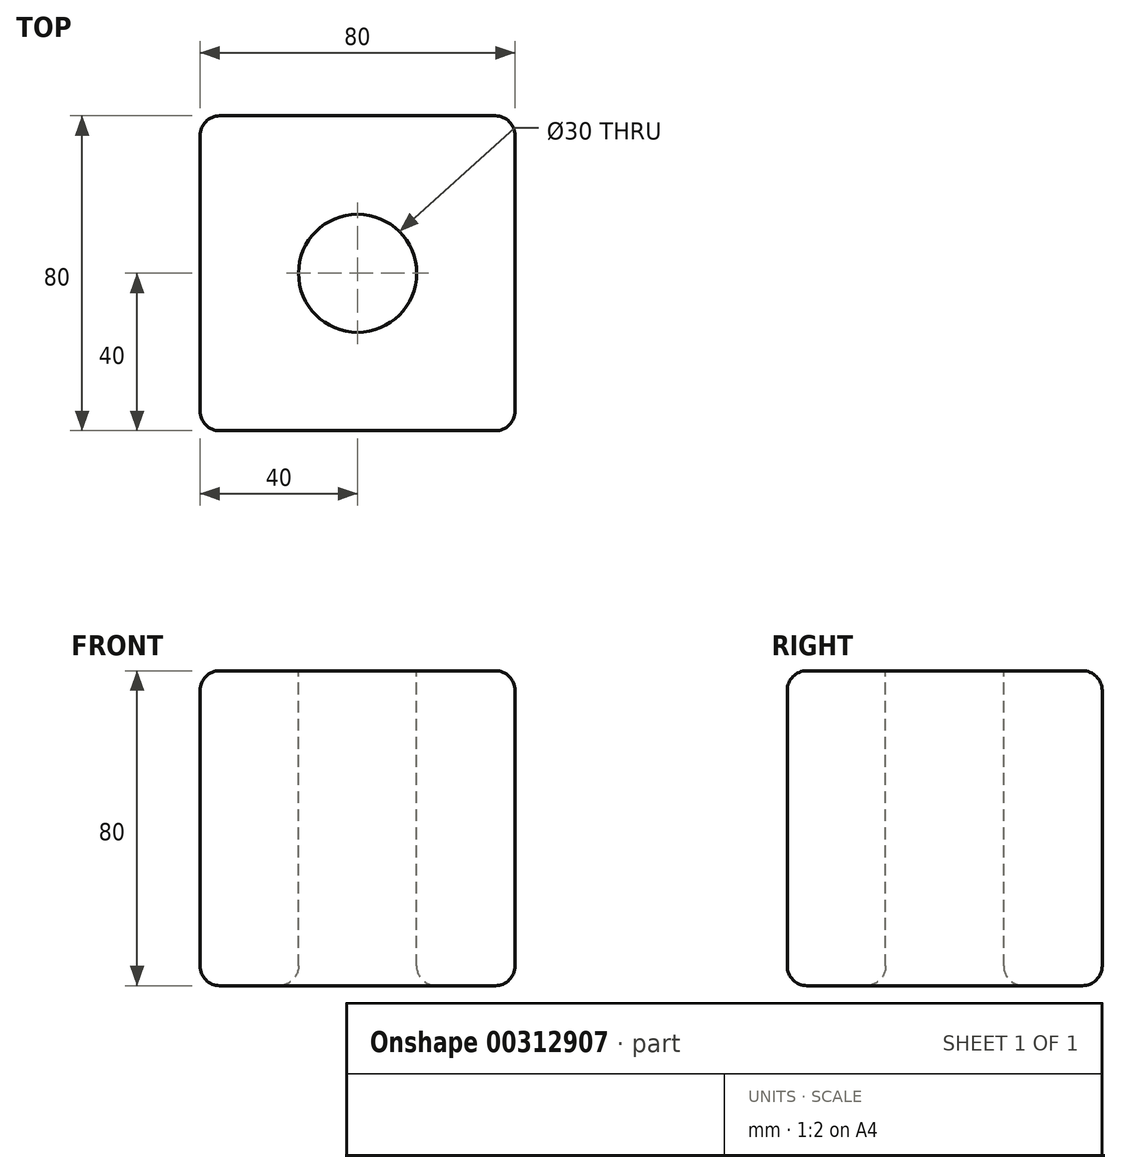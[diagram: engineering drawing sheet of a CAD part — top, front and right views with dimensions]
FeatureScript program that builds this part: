
annotation { "Feature Type Name" : "Feature", "Feature Type Description" : "" }
export const myFeature = defineFeature(function(context is Context, id is Id, definition is map)
    precondition{}
    {
        {
            var Q0;
            Q0=qCreatedBy(makeId("Top.planeOp"),FACE);
            var sketch = newSketch(context, id + "F0", { "sketchPlane" : qUnion([Q0])});
            skLineSegment(sketch, "E0.bottom", {"start": v(-40, 40) * mm, "end": v(40, 40) * mm});
            skLineSegment(sketch, "E0.top", {"start": v(-40, -40) * mm, "end": v(40, -40) * mm});
            skLineSegment(sketch, "E0.left", {"start": v(-40, 40) * mm, "end": v(-40, -40) * mm});
            skLineSegment(sketch, "E0.right", {"start": v(40, 40) * mm, "end": v(40, -40) * mm});
            skPoint(sketch, "E0.middle", {"position": v(0, 0) * mm});
            skSolve(sketch);
        }
        {
            var Q0;
            Q0 = qSketchRegion(id + "F0", true);
            extrude(context, id + "F1", {"entities" : qUnion([Q0]), "endBound" : BoundingType.SYMMETRIC, "depth" : 80 * mm});
        }
        {
            var Q0;
            Q0=makeQuery(id+"F1.opExtrude","CAP_FACE",FACE,{"disambiguationData":[OSD([sQuery(id+"F0.wireOp",EDGE,"E0.bottom"),sQuery(id+"F0.wireOp",EDGE,"E0.top"),sQuery(id+"F0.wireOp",EDGE,"E0.left"),sQuery(id+"F0.wireOp",EDGE,"E0.right")])],"isStart":false});
            var Q1;
            Q1=makeQuery(id+"F1.opExtrude","SWEPT_EDGE",EDGE,{"disambiguationData":[OSD([sQuery(id+"F0.wireOp",EDGE,"E0.top"),sQuery(id+"F0.wireOp",EDGE,"E0.left")])]});
            var Q2;
            Q2=makeQuery(id+"F1.opExtrude","CAP_EDGE",EDGE,{"disambiguationData":[OSD([sQuery(id+"F0.wireOp",EDGE,"E0.top")])],"isStart":false});
            var Q3;
            Q3=makeQuery(id+"F1.opExtrude","SWEPT_EDGE",EDGE,{"disambiguationData":[OSD([sQuery(id+"F0.wireOp",EDGE,"E0.top"),sQuery(id+"F0.wireOp",EDGE,"E0.right")])]});
            var Q4;
            Q4=makeQuery(id+"F1.opExtrude","CAP_EDGE",EDGE,{"disambiguationData":[OSD([sQuery(id+"F0.wireOp",EDGE,"E0.right")])],"isStart":true});
            var Q5;
            Q5=makeQuery(id+"F1.opExtrude","CAP_EDGE",EDGE,{"disambiguationData":[OSD([sQuery(id+"F0.wireOp",EDGE,"E0.top")])],"isStart":true});
            var Q6;
            Q6=makeQuery(id+"F1.opExtrude","CAP_EDGE",EDGE,{"disambiguationData":[OSD([sQuery(id+"F0.wireOp",EDGE,"E0.left")])],"isStart":true});
            var Q7;
            Q7=makeQuery(id+"F1.opExtrude","CAP_FACE",FACE,{"disambiguationData":[OSD([sQuery(id+"F0.wireOp",EDGE,"E0.bottom"),sQuery(id+"F0.wireOp",EDGE,"E0.top"),sQuery(id+"F0.wireOp",EDGE,"E0.left"),sQuery(id+"F0.wireOp",EDGE,"E0.right")])],"isStart":true});
            var Q8;
            Q8=makeQuery(id+"F1.opExtrude","SWEPT_EDGE",EDGE,{"disambiguationData":[OSD([sQuery(id+"F0.wireOp",EDGE,"E0.bottom"),sQuery(id+"F0.wireOp",EDGE,"E0.left")])]});
            var Q9;
            Q9=makeQuery(id+"F1.opExtrude","CAP_EDGE",EDGE,{"disambiguationData":[OSD([sQuery(id+"F0.wireOp",EDGE,"E0.bottom")])],"isStart":false});
            var Q10;
            Q10=makeQuery(id+"F1.opExtrude","SWEPT_EDGE",EDGE,{"disambiguationData":[OSD([sQuery(id+"F0.wireOp",EDGE,"E0.bottom"),sQuery(id+"F0.wireOp",EDGE,"E0.right")])]});
            fillet(context, id + "F2", {"entities" : qUnion([Q0, Q1, Q2, Q3, Q4, Q5, Q6, Q7, Q8, Q9, Q10]), "radius" : 5 * mm, "tangentPropagation" : true, "allowEdgeOverflow" : false});
        }
        {
            var Q0;
            Q0=makeQuery(id+"F1.opExtrude","CAP_FACE",FACE,{"disambiguationData":[OSD([sQuery(id+"F0.wireOp",EDGE,"E0.bottom"),sQuery(id+"F0.wireOp",EDGE,"E0.top"),sQuery(id+"F0.wireOp",EDGE,"E0.left"),sQuery(id+"F0.wireOp",EDGE,"E0.right")])],"isStart":false});
            var sketch = newSketch(context, id + "F3", { "sketchPlane" : qUnion([Q0])});
            skCircle(sketch, "E1", {"center": v(0, 0) * mm, "radius": 15 * mm});
            skSolve(sketch);
        }
        {
            var Q0;
            Q0=makeQuery(id+"F3.imprint","IMPRINT",FACE,{"disambiguationData":[TD([[makeQuery(id+"F3.imprint","IMPRINT",EDGE,{"derivedFrom":sQuery(id+"F3.wireOp",EDGE,"E1")}),1.0]])]});
            extrude(context, id + "F4", {"entities" : qUnion([Q0]), "operationType" : NewBodyOperationType.REMOVE, "endBound" : BoundingType.THROUGH_ALL, "oppositeDirection" : true, "depth" : 25 * mm});
        }
        {
            var Q0;
            Q0=makeQuery(id+"F4.boolean.opBoolean","COPY",EDGE,{"derivedFrom":makeQuery(id+"F4.opExtrude","CAP_EDGE",EDGE,{"disambiguationData":[OSD([sQuery(id+"F3.wireOp",EDGE,"E1")])],"isStart":true})});
            var Q1;
            Q1=makeQuery(id+"F4.boolean.opBoolean","INTERSECT",EDGE,{"derivedFrom":[makeQuery(id+"F1.opExtrude","CAP_FACE",FACE,{"disambiguationData":[OSD([sQuery(id+"F0.wireOp",EDGE,"E0.bottom"),sQuery(id+"F0.wireOp",EDGE,"E0.top"),sQuery(id+"F0.wireOp",EDGE,"E0.left"),sQuery(id+"F0.wireOp",EDGE,"E0.right")])],"isStart":true}),makeQuery(id+"F4.opExtrude","SWEPT_FACE",FACE,{"disambiguationData":[OSD([sQuery(id+"F3.wireOp",EDGE,"E1")])]})]});
            fillet(context, id + "F5", {"entities" : qUnion([Q0, Q1]), "radius" : 5 * mm, "tangentPropagation" : true, "allowEdgeOverflow" : false});
        }
    });
